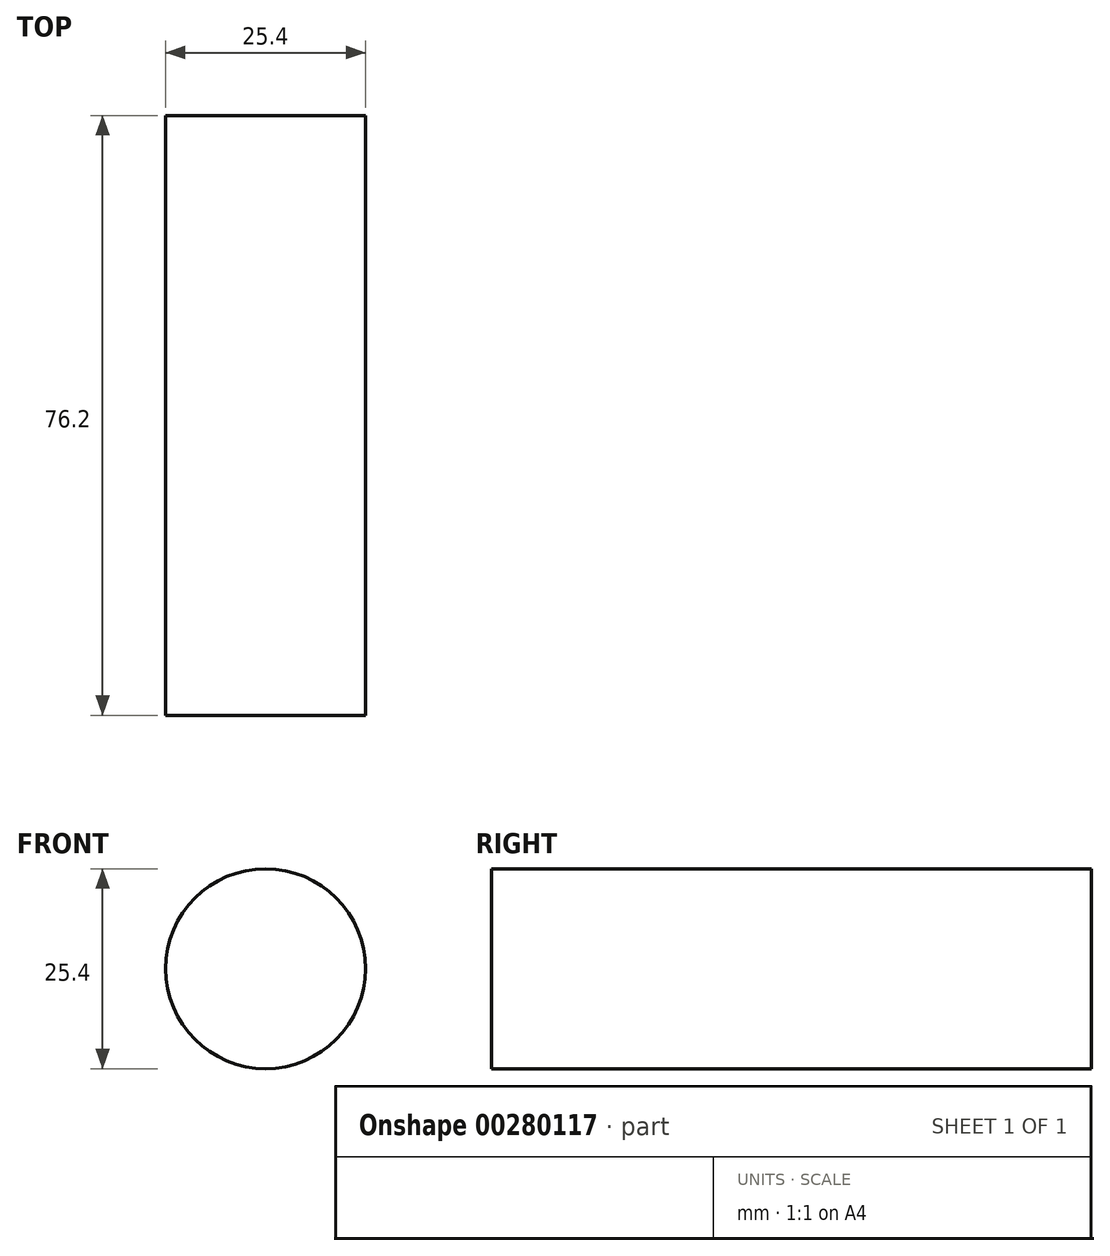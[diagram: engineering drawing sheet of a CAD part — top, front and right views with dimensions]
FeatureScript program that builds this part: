
annotation { "Feature Type Name" : "Feature", "Feature Type Description" : "" }
export const myFeature = defineFeature(function(context is Context, id is Id, definition is map)
    precondition{}
    {
        {
            var Q0;
            Q0=qCreatedBy(makeId("Front.planeOp"),FACE);
            var sketch = newSketch(context, id + "F0", { "sketchPlane" : qUnion([Q0])});
            skCircle(sketch, "E0", {"center": v(-32.27, 25.78) * mm, "radius": 12.7 * mm});
            skSolve(sketch);
        }
        {
            var Q0;
            Q0 = qSketchRegion(id + "F0", true);
            extrude(context, id + "F1", {"entities" : qUnion([Q0]), "depth" : 76.2 * mm});
        }
    });
